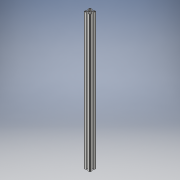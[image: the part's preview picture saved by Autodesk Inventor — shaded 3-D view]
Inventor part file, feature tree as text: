
AUTODESK INVENTOR PART (.ipt)
format: ipt  version: 2016 (Build 200138000, 138)  size: 1,120,768 bytes
history: native  units: in
note: dims shown in document units (in); Inventor stores cm internally (conversion verified against a paired STEP export)
features: extrude x1, sketch x1
ambient origin geometry x8: Origin, YZ Plane, XZ Plane, XY Plane, X Axis, Y Axis, Z Axis, Center Point
bodies: Solid1 (feature_tree)
feature tree (2):
  extrude  "Extrusion1"  [1 undecoded]
  sketch  "Sketch1"  dims[d0=26.7717in d1=0.0in]
note: 1 required parameter value undecoded (feature->parameter linkage not recoverable at this tier; creation-order binding heuristic only, values carry confidence <= 0.55)
